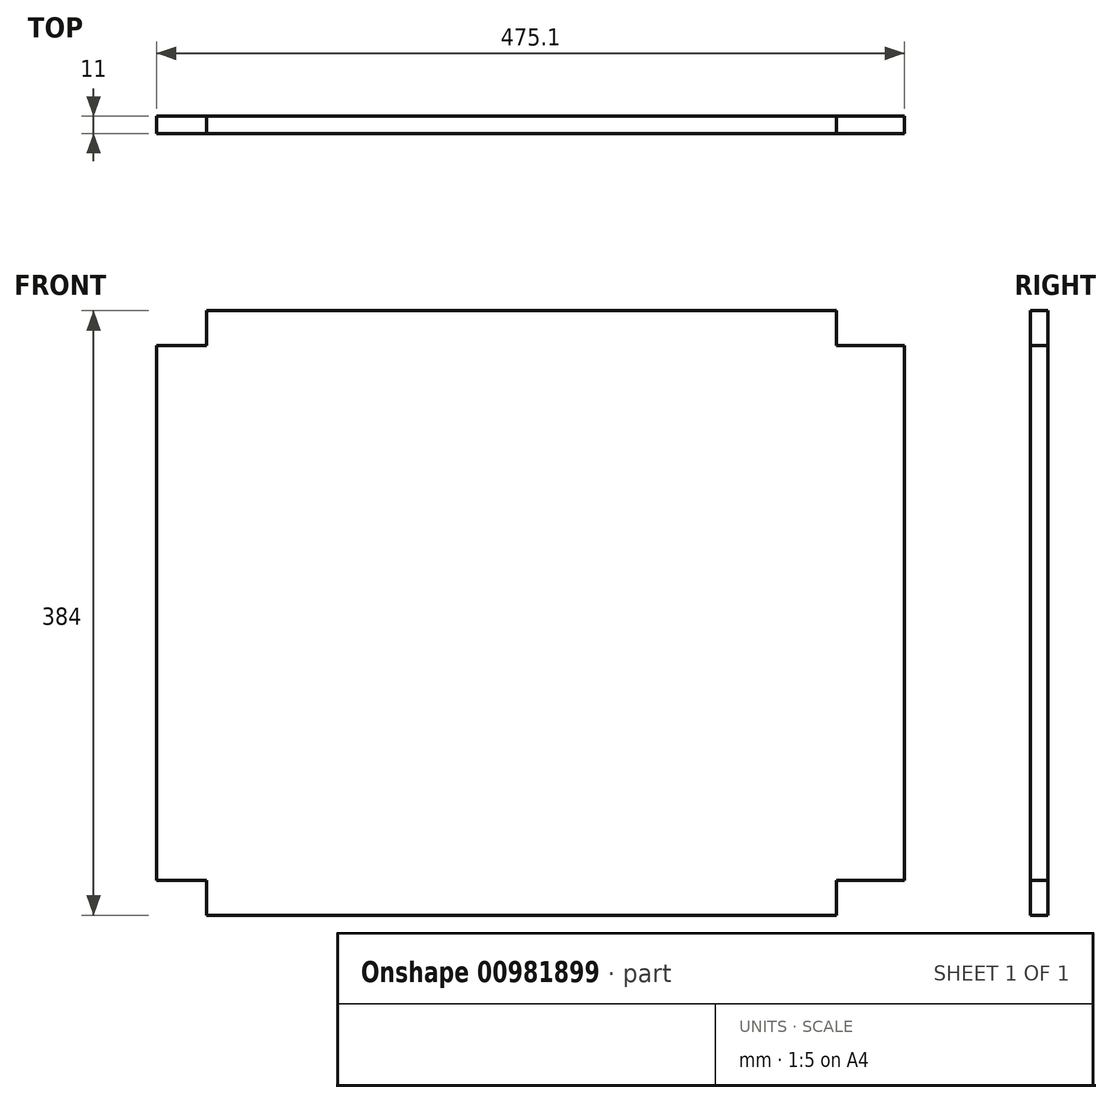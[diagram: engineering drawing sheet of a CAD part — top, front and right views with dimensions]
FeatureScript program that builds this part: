
annotation { "Feature Type Name" : "Feature", "Feature Type Description" : "" }
export const myFeature = defineFeature(function(context is Context, id is Id, definition is map)
    precondition{}
    {
        {
            var Q0;
            Q0=qCreatedBy(makeId("Front.planeOp"),FACE);
            var sketch = newSketch(context, id + "F0", { "sketchPlane" : qUnion([Q0])});
            skLineSegment(sketch, "E0", {"start": v(237.55, -170) * mm, "end": v(237.55, 170) * mm});
            skLineSegment(sketch, "E1", {"start": v(237.55, -170) * mm, "end": v(194.16, -170) * mm});
            skLineSegment(sketch, "E2", {"start": v(-205.84, -170) * mm, "end": v(-237.55, -170) * mm});
            skLineSegment(sketch, "E3", {"start": v(194.16, -192) * mm, "end": v(-205.84, -192) * mm});
            skLineSegment(sketch, "E4", {"start": v(237.55, 170) * mm, "end": v(194.16, 170) * mm});
            skLineSegment(sketch, "E5", {"start": v(-205.84, 170) * mm, "end": v(-237.55, 170) * mm});
            skLineSegment(sketch, "E6", {"start": v(194.16, 192) * mm, "end": v(-205.84, 192) * mm});
            skLineSegment(sketch, "E7", {"start": v(194.16, 192) * mm, "end": v(194.16, 170) * mm});
            skLineSegment(sketch, "E8", {"start": v(194.16, -170) * mm, "end": v(194.16, -192) * mm});
            skLineSegment(sketch, "E9", {"start": v(-205.84, 192) * mm, "end": v(-205.84, 170) * mm});
            skLineSegment(sketch, "E10", {"start": v(-205.84, -170) * mm, "end": v(-205.84, -192) * mm});
            skLineSegment(sketch, "E11", {"start": v(-237.55, -170) * mm, "end": v(-237.55, 170) * mm});
            skSolve(sketch);
        }
        {
            var Q0;
            Q0=makeQuery(id+"F0.imprint","IMPRINT",FACE,{"disambiguationData":[TD([[makeQuery(id+"F0.imprint","IMPRINT",EDGE,{"derivedFrom":sQuery(id+"F0.wireOp",EDGE,"E0")}),1.0]])]});
            extrude(context, id + "F1", {"entities" : qUnion([Q0]), "depth" : 11 * mm, "offsetDistance" : 25 * mm});
        }
    });
